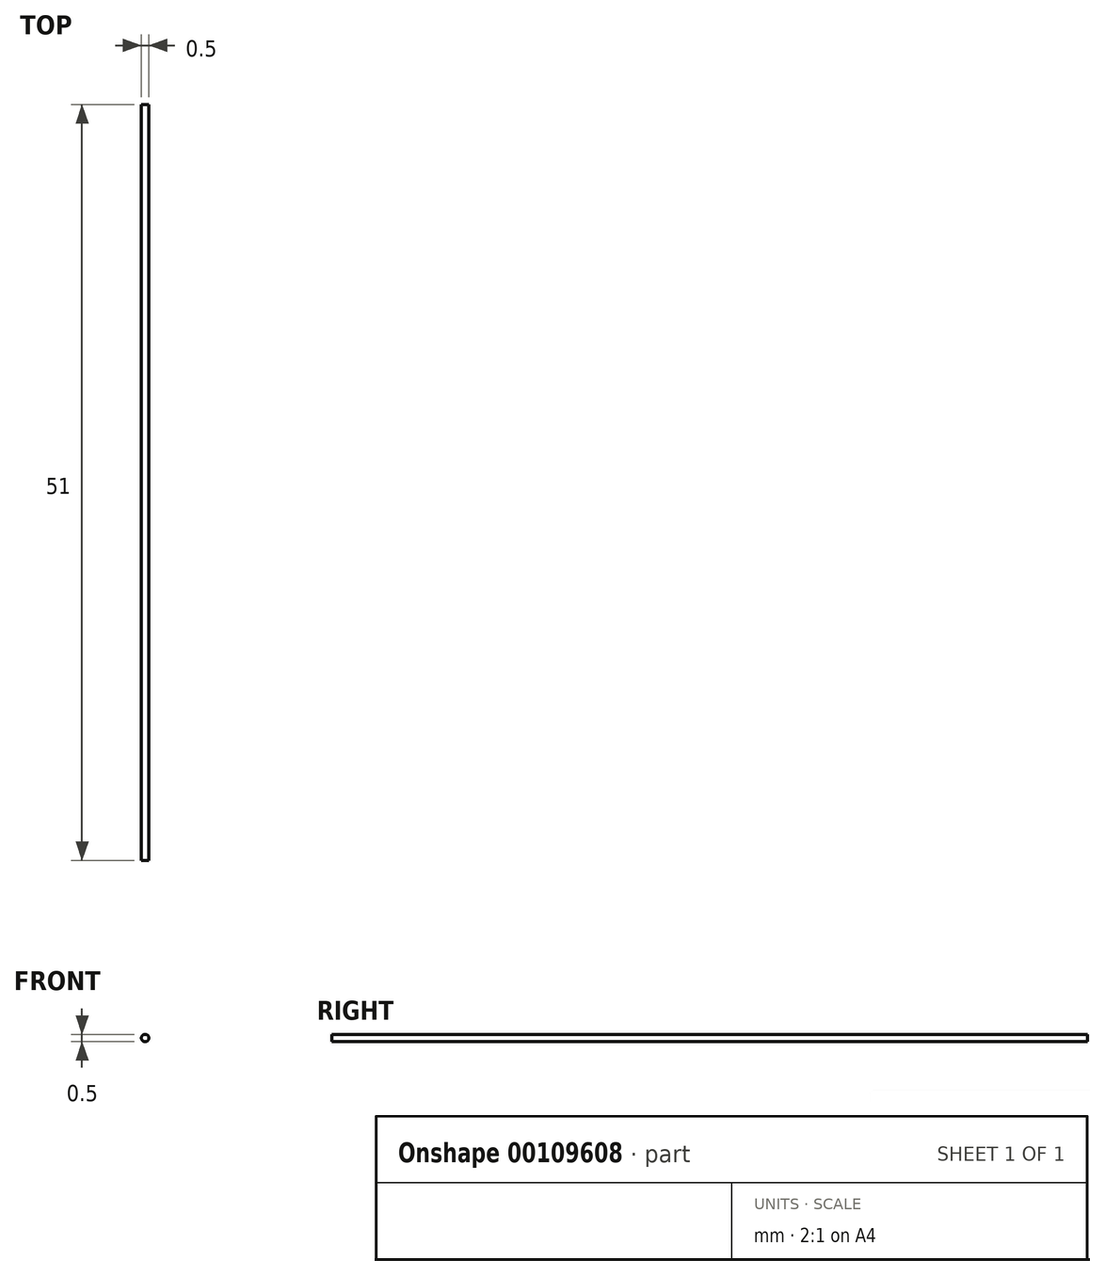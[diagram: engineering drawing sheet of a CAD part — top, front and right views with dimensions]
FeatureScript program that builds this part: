
annotation { "Feature Type Name" : "Feature", "Feature Type Description" : "" }
export const myFeature = defineFeature(function(context is Context, id is Id, definition is map)
    precondition{}
    {
        {
            var Q0;
            Q0=qCreatedBy(makeId("Front.planeOp"),FACE);
            var sketch = newSketch(context, id + "F0", { "sketchPlane" : qUnion([Q0])});
            skCircle(sketch, "E0", {"center": v(0, 0) * mm, "radius": 0.25 * mm});
            skSolve(sketch);
        }
        {
            var Q0;
            Q0=qCreatedBy(makeId("Top.planeOp"),FACE);
            var sketch = newSketch(context, id + "F1", { "sketchPlane" : qUnion([Q0])});
            skLineSegment(sketch, "E1", {"start": v(0, 0) * mm, "end": v(0, -51) * mm});
            skSolve(sketch);
        }
        {
            var Q0;
            Q0 = qSketchRegion(id + "F0", true);
            var Q1;
            Q1 = qConstructionFilter(qBodyType(qCreatedBy(id + "F1" ,EDGE), BodyType.WIRE), ConstructionObject.NO);
            sweep(context, id + "F2", {"profiles" : qUnion([Q0]), "path" : qUnion([Q1])});
        }
    });
